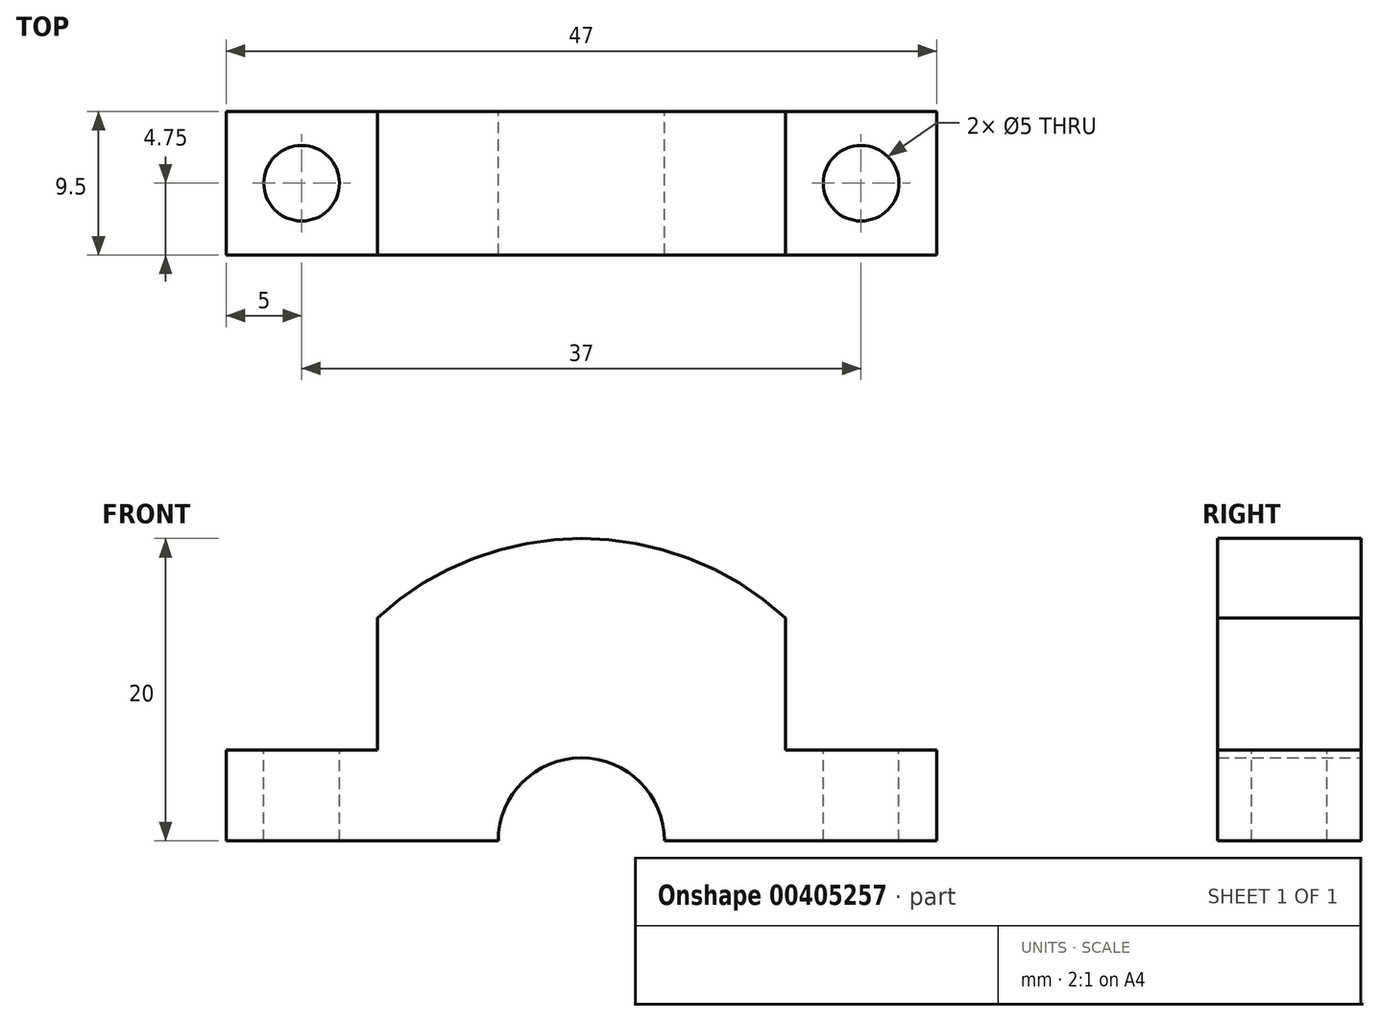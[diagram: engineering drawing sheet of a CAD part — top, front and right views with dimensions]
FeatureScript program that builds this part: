
annotation { "Feature Type Name" : "Feature", "Feature Type Description" : "" }
export const myFeature = defineFeature(function(context is Context, id is Id, definition is map)
    precondition{}
    {
        {
            var Q0;
            Q0=qCreatedBy(makeId("Front.planeOp"),FACE);
            var sketch = newSketch(context, id + "F0", { "sketchPlane" : qUnion([Q0])});
            skLineSegment(sketch, "E0", {"start": v(-23.5, 0) * mm, "end": v(-5.5, 0) * mm});
            skArc(sketch, "E1", {"start": v(5.5, 0) * mm, "mid": v(0, 5.5) * mm, "end": v(-5.5, 0) * mm});
            skLineSegment(sketch, "E2", {"start": v(5.5, 0) * mm, "end": v(23.5, 0) * mm});
            skLineSegment(sketch, "E3", {"start": v(23.5, 0) * mm, "end": v(23.5, 6) * mm});
            skLineSegment(sketch, "E4", {"start": v(23.5, 6) * mm, "end": v(13.5, 6) * mm});
            skLineSegment(sketch, "E5", {"start": v(13.5, 6) * mm, "end": v(13.5, 14.76) * mm});
            skLineSegment(sketch, "E6", {"start": v(-23.5, 0) * mm, "end": v(-23.5, 6) * mm});
            skLineSegment(sketch, "E7", {"start": v(-23.5, 6) * mm, "end": v(-13.5, 6) * mm});
            skLineSegment(sketch, "E8", {"start": v(-13.5, 6) * mm, "end": v(-13.5, 14.76) * mm});
            skArc(sketch, "E9", {"start": v(13.5, 14.76) * mm, "mid": v(0, 20) * mm, "end": v(-13.5, 14.76) * mm});
            skSolve(sketch);
        }
        {
            var Q0;
            Q0=makeQuery(id+"F0.imprint","IMPRINT",FACE,{"disambiguationData":[TD([[makeQuery(id+"F0.imprint","IMPRINT",EDGE,{"derivedFrom":sQuery(id+"F0.wireOp",EDGE,"E0")}),1.0]])]});
            extrude(context, id + "F1", {"entities" : qUnion([Q0]), "endBound" : BoundingType.SYMMETRIC, "depth" : 9.5 * mm});
        }
        {
            var Q0;
            Q0=makeQuery(id+"F1.opExtrude","SWEPT_FACE",FACE,{"disambiguationData":[OSD([sQuery(id+"F0.wireOp",EDGE,"E7")])]});
            var sketch = newSketch(context, id + "F2", { "sketchPlane" : qUnion([Q0])});
            skCircle(sketch, "E10", {"center": v(-18.5, 0) * mm, "radius": 2.5 * mm});
            skCircle(sketch, "E11", {"center": v(18.5, 0) * mm, "radius": 2.5 * mm});
            skSolve(sketch);
        }
        {
            var Q0;
            Q0=qSketchRegion(id+"F2",true);
            extrude(context, id + "F3", {"entities" : qUnion([Q0]), "operationType" : NewBodyOperationType.REMOVE, "endBound" : BoundingType.THROUGH_ALL, "oppositeDirection" : true, "depth" : 25 * mm});
        }
    });
